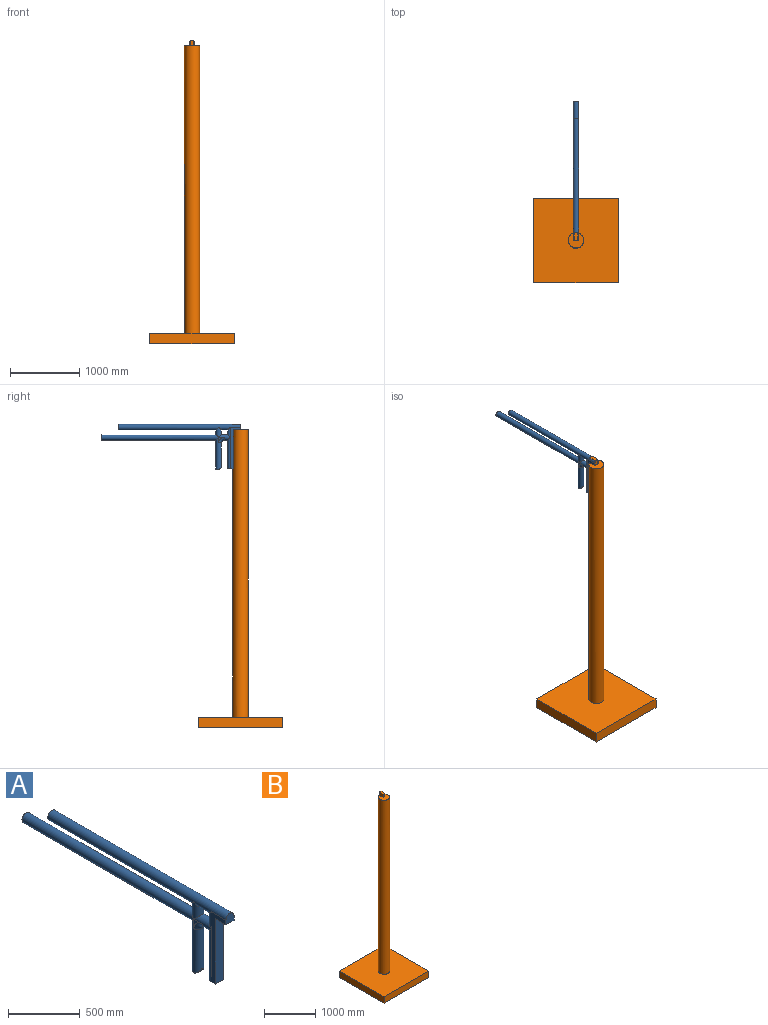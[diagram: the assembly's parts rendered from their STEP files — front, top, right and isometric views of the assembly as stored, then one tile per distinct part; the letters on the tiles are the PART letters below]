
ASSEMBLY  parts=2 mates=1
PART A: 20 faces, bbox 80x2011.4x646.1 mm
  f0: plane 80x80mm, normal (-1,0,0), area 1373.5mm2, adj f14,f18,f19
  f1: plane 80x80mm, normal (1,0,0), area 1373.5mm2, adj f14,f18,f19
  f2: plane 80x80mm, normal (0,-1,0), area 5713.3mm2, adj f3,f9,f10,f11
  f3: plane 106.65x80mm, normal (0,0,-1), area 8531.7mm2, adj f2,f4,f9,f10
  f4: plane 558.94x80mm, normal (0,-1,0), area 44715.3mm2, adj f3,f5,f9,f10
  f5: plane 80x80mm, normal (0,0,-1), area 5713.3mm2, adj f4,f9,f10,f17
  f6: plane 80x40mm, normal (0,0,-1), area 2513.3mm2, adj f14,f15
  f7: plane 80x80mm, normal (0,1,0), area 5026.5mm2, adj f12
  f8: plane 80x80mm, normal (0,1,0), area 5026.5mm2, adj f11
  f9: plane 598.94x146.65mm, normal (-1,0,0), area 28223.5mm2, adj f2,f3,f4,f5,f11,f16,f17
  f10: plane 598.94x146.65mm, normal (1,0,0), area 28223.5mm2, adj f2,f3,f4,f5,f11,f16,f17
  f11: cylinder r=40mm len=1757.36mm, axis (0,-1,0), area 413645.2mm2, adj f2,f8,f9,f10,f13,f16
  f12: cylinder r=40mm len=1695.48mm, axis (0,-1,0), area 419720.2mm2, adj f7,f13,f14
  f13: cylinder r=40mm len=148.6mm, axis (0,0,1), area 24547.3mm2, adj f11,f12,f18
  f14: cylinder r=40mm len=457.49mm, axis (0,0,1), area 99898.9mm2, adj f0,f1,f6,f12,f15,f19
  f15: cylinder r=40mm len=80mm, axis (1,0,0), area 3200mm2, adj f6,f14
  f16: cylinder r=40mm len=148.6mm, axis (0,0,1), area 12273.6mm2, adj f9,f10,f11,f18
  f17: cylinder r=40mm len=450.34mm, axis (0,0,1), area 53391.5mm2, adj f5,f9,f10,f18
  f18: cylinder r=40mm len=169.24mm, axis (0,-1,0), area 22880.9mm2, adj f0,f1,f13,f16,f17,f19
  f19: torus R=80mm, axis (1,0,0), area 10764.8mm2, adj f0,f1,f14,f18
PART B: 12 faces, bbox 1219.2x1219.2x4383.1 mm
  f0: plane 106.65x80mm, normal (-1,0,0), area 8531.7mm2, adj f2,f9,f10,f11
  f1: plane 106.65x80mm, normal (1,0,0), area 8531.7mm2, adj f2,f9,f10,f11
  f2: plane 109.54x50mm, normal (0,0,1), area 5428.9mm2, adj f0,f1,f10,f11
  f3: plane 1219.2x1219.2mm, normal (0,0,1), area 1448754.4mm2, adj f4,f6,f7,f8,f10
  f4: plane 1219.2x152.4mm, normal (-1,0,0), area 185806.1mm2, adj f3,f5,f7,f8
  f5: plane 1219.2x1219.2mm, normal (0,0,-1), area 1486448.6mm2, adj f4,f6,f7,f8
  f6: plane 1219.2x152.4mm, normal (1,0,0), area 185806.1mm2, adj f3,f5,f7,f8
  f7: plane 1219.2x152.4mm, normal (0,-1,0), area 185806.1mm2, adj f3,f4,f5,f6
  f8: plane 1219.2x152.4mm, normal (0,1,0), area 185806.1mm2, adj f3,f4,f5,f6
  f9: plane 219.08x216.18mm, normal (0,0,1), area 32265.3mm2, adj f0,f1,f10,f11
  f10: cylinder r=109.54mm len=4230.69mm, axis (0,0,1), area 2860723mm2, adj f0,f1,f2,f3,f9
  f11: plane 80x50mm, normal (0,-1,0), area 4000mm2, adj f0,f1,f2,f9
PLACE A t=(-653.08,-1607.56,-2880.91)mm
PLACE B t=(-653.08,-1607.56,-2880.91)mm fixed
MATE revolute B.f10 <-> A.f3  axis (0,0,1) through (-43.48,-1607.56,1422.18)mm
